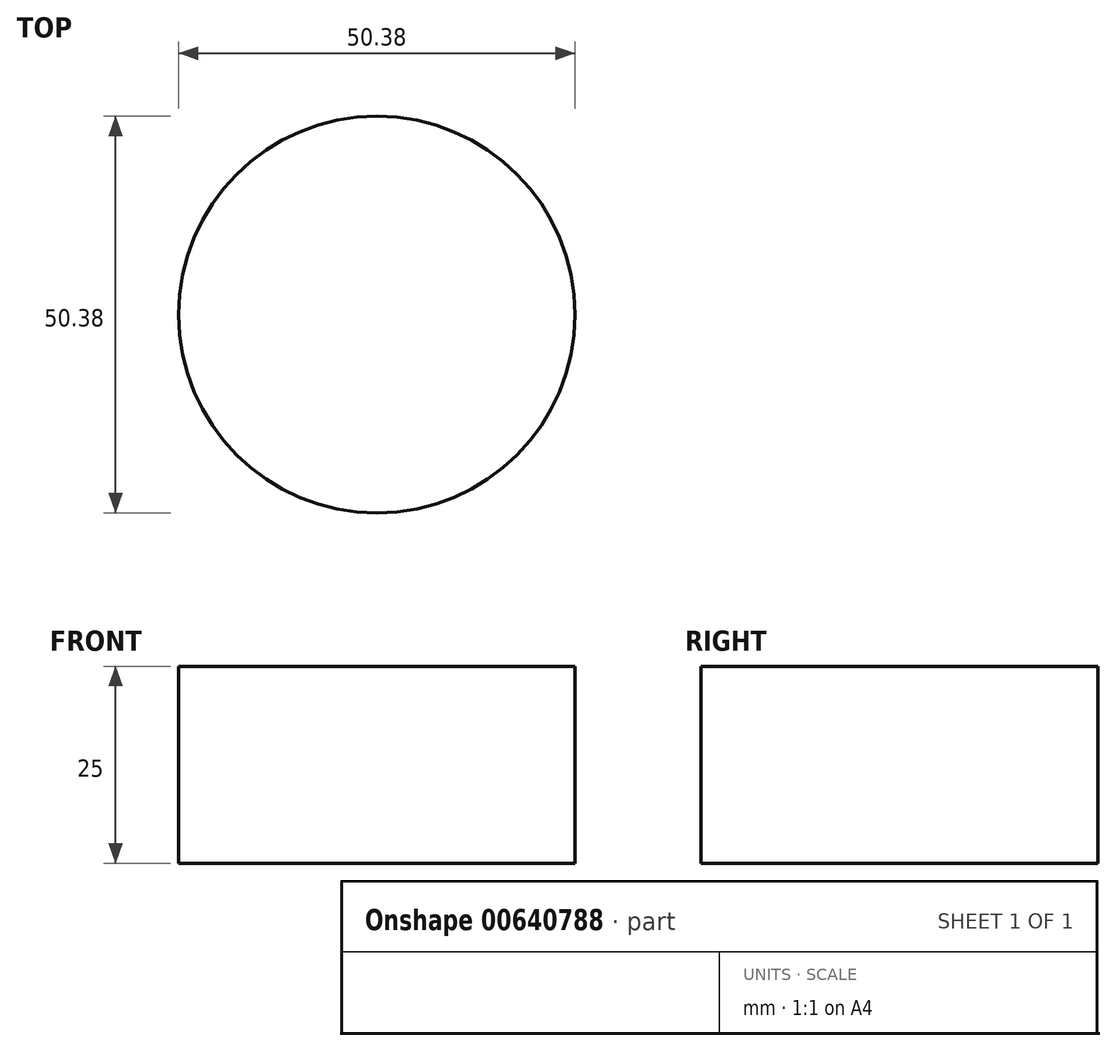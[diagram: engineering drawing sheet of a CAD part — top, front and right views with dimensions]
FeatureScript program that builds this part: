
annotation { "Feature Type Name" : "Feature", "Feature Type Description" : "" }
export const myFeature = defineFeature(function(context is Context, id is Id, definition is map)
    precondition{}
    {
        {
            var Q0;
            Q0=qCreatedBy(makeId("Top.planeOp"),FACE);
            var sketch = newSketch(context, id + "F0", { "sketchPlane" : qUnion([Q0])});
            skCircle(sketch, "E0", {"center": v(0, 0) * mm, "radius": 25.2 * mm});
            skSolve(sketch);
        }
        {
            var Q0;
            Q0 = qSketchRegion(id + "F0", true);
            extrude(context, id + "F1", {"entities" : qUnion([Q0]), "depth" : 25 * mm, "offsetDistance" : 25 * mm});
        }
    });
